# Revit family: AD-C42T
name_source: partatom
category: Communication Devices
revit_build: Autodesk Revit Architecture 2012 (Build: 20110309_2315(x64)
units: mm (PartAtom-declared; Revit-internal decimal feet)

## types (1)
- AD-C42T
    100V Taps = 30, 15, 7.5
    70V Taps = 30, 15, 7.5, 3.8
    Coverage Horizontal = 90.00°
    Coverage Vertical = 90.00°
    Default Elevation = 48"
    Depth = 9.3"
    Description = 4" Compact 2-way Loudspeaker Element
    Enclosure Depth = 8.317"
    Enclosure Radius = 3.242"
    Grille Depth = 0.4"
    Grille Radius Base = 3.75"
    Grille Radius Extent = 2.51"
    Impedance = 8
    Manufacturer = QSC Audio Products, LLC
    Manufacturer URL = www.qscaudio.com
    Middle Depth = 0.583"
    Middle Radius = 3.35"
    Model = AD-C42T
    Power Handling = 40
    Product Documentation Link = http://media.qscaudio.com
    Product Page URL = http://www.qscaudio.com
    Regulatory Compliance = RoHS, UL1480, UL2043
    SPL Max = 110
    Sensitivity = 88
    URL = http://www.qscaudio.com
    Weight Dimensional (kg) = 8.2
    Weight Dimensional (lb) = 18
    Weight Product (kg) = 2.7
    Weight Product (lb) = 6.1
    Width = 7.5"

## geometry (parser evidence)
native form markers: Blend x2, Sweep x1
no freeform markers — native parametric forms only
